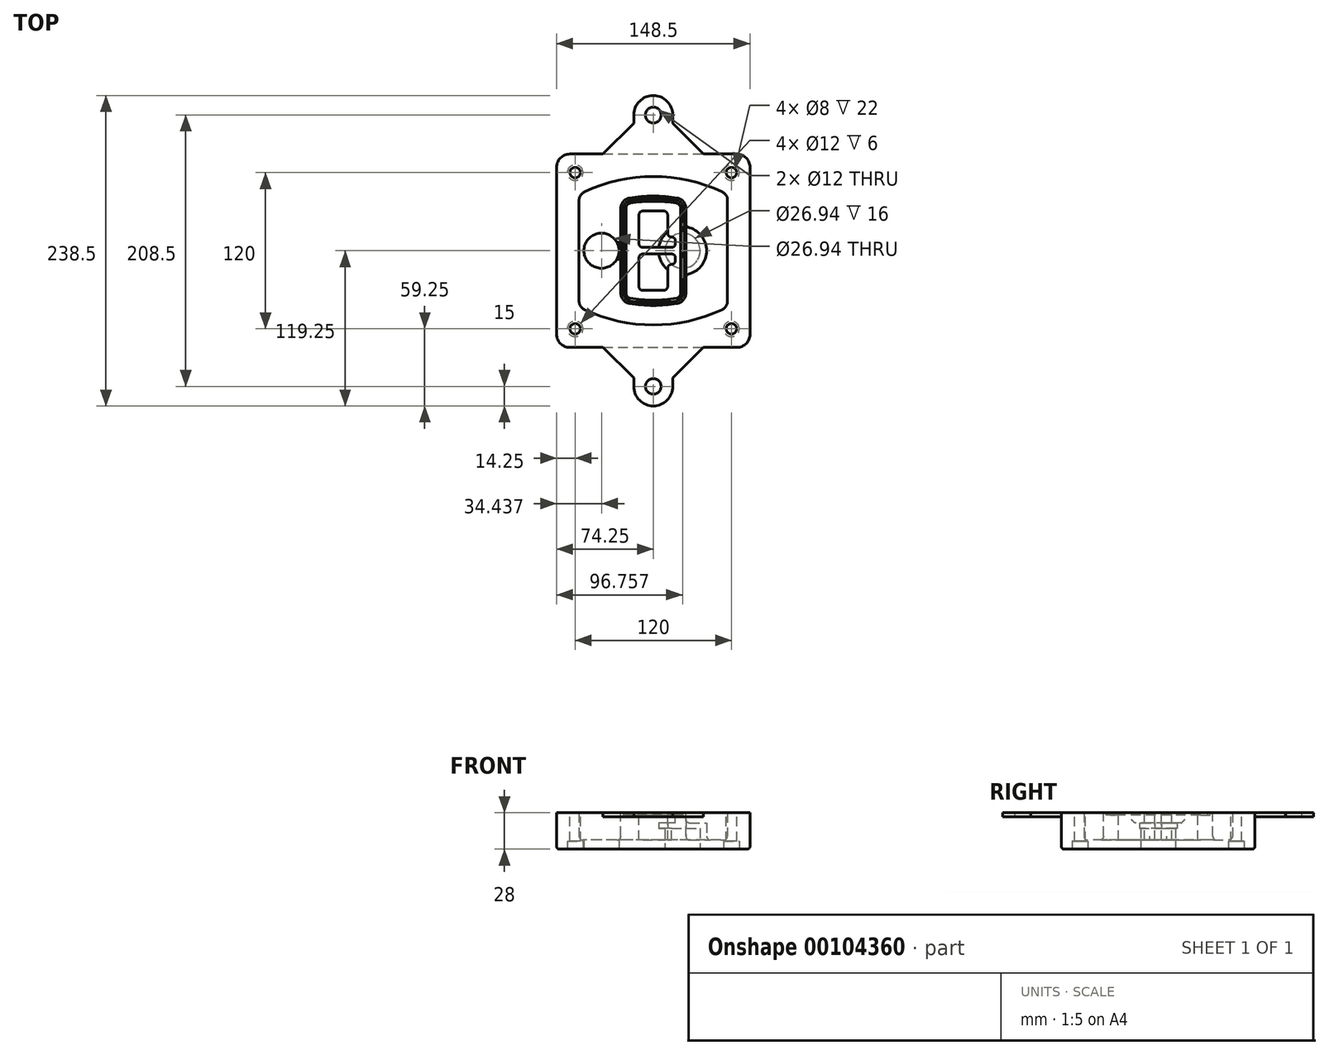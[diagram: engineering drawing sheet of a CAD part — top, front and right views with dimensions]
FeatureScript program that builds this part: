
annotation { "Feature Type Name" : "Feature", "Feature Type Description" : "" }
export const myFeature = defineFeature(function(context is Context, id is Id, definition is map)
    precondition{}
    {
        {
            var Q0;
            Q0=qCreatedBy(makeId("Top.planeOp"),FACE);
            var sketch = newSketch(context, id + "F0", { "sketchPlane" : qUnion([Q0])});
            skPoint(sketch, "E0.rect.middle", {"position": v(0, 0) * mm});
            skLineSegment(sketch, "E1.bottom", {"start": v(-64.25, -74.25) * mm, "end": v(64.25, -74.25) * mm});
            skLineSegment(sketch, "E1.top", {"start": v(-64.25, 74.25) * mm, "end": v(64.25, 74.25) * mm});
            skLineSegment(sketch, "E1.left", {"start": v(-74.25, -64.25) * mm, "end": v(-74.25, 64.25) * mm});
            skLineSegment(sketch, "E1.right", {"start": v(74.25, -64.25) * mm, "end": v(74.25, 64.25) * mm});
            skLineSegment(sketch, "E2", {"start": v(-74.25, 74.25) * mm, "end": v(74.25, -74.25) * mm, "construction": true});
            skLineSegment(sketch, "E3", {"start": v(74.25, 74.25) * mm, "end": v(-74.25, -74.25) * mm, "construction": true});
            skCircle(sketch, "E4", {"center": v(-60, 60) * mm, "radius": 4 * mm});
            skCircle(sketch, "E5", {"center": v(60, 60) * mm, "radius": 4 * mm});
            skCircle(sketch, "E6", {"center": v(60, -60) * mm, "radius": 4 * mm});
            skCircle(sketch, "E7", {"center": v(-60, -60) * mm, "radius": 4 * mm});
            skLineSegment(sketch, "E8", {"start": v(-60, 60) * mm, "end": v(60, 60) * mm, "construction": true});
            skLineSegment(sketch, "E9", {"start": v(60, 60) * mm, "end": v(60, -60) * mm, "construction": true});
            skLineSegment(sketch, "E10", {"start": v(60, -60) * mm, "end": v(-60, -60) * mm, "construction": true});
            skLineSegment(sketch, "E11", {"start": v(-60, -60) * mm, "end": v(-60, 60) * mm, "construction": true});
            skLineSegment(sketch, "E12", {"start": v(-60, 38.83) * mm, "end": v(-60, -38.83) * mm});
            skLineSegment(sketch, "E13", {"start": v(60, 38.83) * mm, "end": v(60, -38.83) * mm});
            skArc(sketch, "E14", {"start": v(54.26, 47.88) * mm, "mid": v(0, 60) * mm, "end": v(-54.26, 47.88) * mm});
            skArc(sketch, "E15", {"start": v(-54.26, -47.88) * mm, "mid": v(0, -60) * mm, "end": v(54.26, -47.88) * mm});
            skLineSegment(sketch, "E16", {"start": v(-60, 0) * mm, "end": v(60, 0) * mm, "construction": true});
            skPoint(sketch, "E17.visualSharp", {"position": v(-60, -45) * mm});
            skArc(sketch, "E17.filletArc", {"start": v(-60, -38.83) * mm, "mid": v(-58.44, -44.2) * mm, "end": v(-54.26, -47.88) * mm});
            skPoint(sketch, "E18.visualSharp", {"position": v(-60, 45) * mm});
            skArc(sketch, "E18.filletArc", {"start": v(-54.26, 47.88) * mm, "mid": v(-58.44, 44.2) * mm, "end": v(-60, 38.83) * mm});
            skPoint(sketch, "E19.visualSharp", {"position": v(60, 45) * mm});
            skArc(sketch, "E19.filletArc", {"start": v(60, 38.83) * mm, "mid": v(58.44, 44.2) * mm, "end": v(54.26, 47.88) * mm});
            skPoint(sketch, "E20.visualSharp", {"position": v(60, -45) * mm});
            skArc(sketch, "E20.filletArc", {"start": v(54.26, -47.88) * mm, "mid": v(58.44, -44.2) * mm, "end": v(60, -38.83) * mm});
            skPoint(sketch, "E21.visualSharp", {"position": v(-74.25, 74.25) * mm});
            skArc(sketch, "E21.filletArc", {"start": v(-64.25, 74.25) * mm, "mid": v(-71.32, 71.32) * mm, "end": v(-74.25, 64.25) * mm});
            skPoint(sketch, "E22.visualSharp", {"position": v(74.25, 74.25) * mm});
            skArc(sketch, "E22.filletArc", {"start": v(74.25, 64.25) * mm, "mid": v(71.32, 71.32) * mm, "end": v(64.25, 74.25) * mm});
            skPoint(sketch, "E23.visualSharp", {"position": v(74.25, -74.25) * mm});
            skArc(sketch, "E23.filletArc", {"start": v(64.25, -74.25) * mm, "mid": v(71.32, -71.32) * mm, "end": v(74.25, -64.25) * mm});
            skPoint(sketch, "E24.visualSharp", {"position": v(-74.25, -74.25) * mm});
            skArc(sketch, "E24.filletArc", {"start": v(-74.25, -64.25) * mm, "mid": v(-71.32, -71.32) * mm, "end": v(-64.25, -74.25) * mm});
            skArc(sketch, "E25.0", {"start": v(57, 38.83) * mm, "mid": v(55.9, 42.58) * mm, "end": v(52.98, 45.17) * mm});
            skLineSegment(sketch, "E25.1", {"start": v(57, 38.83) * mm, "end": v(57, -38.83) * mm});
            skArc(sketch, "E25.2", {"start": v(52.98, -45.17) * mm, "mid": v(55.9, -42.58) * mm, "end": v(57, -38.83) * mm});
            skArc(sketch, "E25.3", {"start": v(-52.98, -45.17) * mm, "mid": v(0, -57) * mm, "end": v(52.98, -45.17) * mm});
            skArc(sketch, "E25.4", {"start": v(-57, -38.83) * mm, "mid": v(-55.9, -42.58) * mm, "end": v(-52.98, -45.17) * mm});
            skArc(sketch, "E25.5", {"start": v(52.98, 45.17) * mm, "mid": v(0, 57) * mm, "end": v(-52.98, 45.17) * mm});
            skLineSegment(sketch, "E25.6", {"start": v(-57, 38.83) * mm, "end": v(-57, -38.83) * mm});
            skArc(sketch, "E25.7", {"start": v(-52.98, 45.17) * mm, "mid": v(-55.9, 42.58) * mm, "end": v(-57, 38.83) * mm});
            skArc(sketch, "E26.0", {"start": v(-55.96, 51.5) * mm, "mid": v(-61.82, 46.33) * mm, "end": v(-64, 38.83) * mm});
            skArc(sketch, "E26.1", {"start": v(55.96, 51.5) * mm, "mid": v(0, 64) * mm, "end": v(-55.96, 51.5) * mm});
            skArc(sketch, "E26.2", {"start": v(64, 38.83) * mm, "mid": v(61.82, 46.33) * mm, "end": v(55.96, 51.5) * mm});
            skLineSegment(sketch, "E26.3", {"start": v(64, 38.83) * mm, "end": v(64, -38.83) * mm});
            skArc(sketch, "E26.4", {"start": v(55.96, -51.5) * mm, "mid": v(61.82, -46.33) * mm, "end": v(64, -38.83) * mm});
            skLineSegment(sketch, "E26.5", {"start": v(-64, 38.83) * mm, "end": v(-64, -38.83) * mm});
            skArc(sketch, "E26.6", {"start": v(-55.96, -51.5) * mm, "mid": v(0, -64) * mm, "end": v(55.96, -51.5) * mm});
            skArc(sketch, "E26.7", {"start": v(-64, -38.83) * mm, "mid": v(-61.82, -46.33) * mm, "end": v(-55.96, -51.5) * mm});
            skSolve(sketch);
        }
        {
            var Q0;
            Q0=makeQuery(id+"F0.imprint","IMPRINT",FACE,{"disambiguationData":[TD([[makeQuery(id+"F0.imprint","IMPRINT",EDGE,{"derivedFrom":sQuery(id+"F0.wireOp",EDGE,"E1.bottom")}),1.0]])]});
            var Q1;
            Q1=makeQuery(id+"F0.imprint","IMPRINT",FACE,{"disambiguationData":[TD([[makeQuery(id+"F0.imprint","IMPRINT",EDGE,{"derivedFrom":sQuery(id+"F0.wireOp",EDGE,"E12")}),1.0]])]});
            var Q2;
            Q2=makeQuery(id+"F0.imprint","IMPRINT",FACE,{"disambiguationData":[TD([[makeQuery(id+"F0.imprint","IMPRINT",EDGE,{"derivedFrom":sQuery(id+"F0.wireOp",EDGE,"E25.0")}),1.0]])]});
            var Q3;
            Q3=makeQuery(id+"F0.imprint","IMPRINT",FACE,{"disambiguationData":[TD([[makeQuery(id+"F0.imprint","IMPRINT",EDGE,{"derivedFrom":sQuery(id+"F0.wireOp",EDGE,"E12")}),-1.0]])]});
            extrude(context, id + "F1", {"entities" : qUnion([Q0, Q1, Q2, Q3]), "oppositeDirection" : true, "depth" : 25 * mm});
        }
        {
            var Q0;
            Q0=makeQuery(id+"F0.imprint","IMPRINT",FACE,{"disambiguationData":[TD([[makeQuery(id+"F0.imprint","IMPRINT",EDGE,{"derivedFrom":sQuery(id+"F0.wireOp",EDGE,"E12")}),1.0]])]});
            extrude(context, id + "F2", {"entities" : qUnion([Q0]), "operationType" : NewBodyOperationType.ADD, "depth" : 3 * mm});
        }
        {
            var Q0;
            Q0=makeQuery(id+"F0.imprint","IMPRINT",FACE,{"disambiguationData":[TD([[makeQuery(id+"F0.imprint","IMPRINT",EDGE,{"derivedFrom":sQuery(id+"F0.wireOp",EDGE,"E25.0")}),1.0]])]});
            extrude(context, id + "F3", {"entities" : qUnion([Q0]), "operationType" : NewBodyOperationType.REMOVE, "oppositeDirection" : true, "depth" : 18 * mm});
        }
        {
            var Q0;
            Q0=makeQuery(id+"F2.opExtrude","CAP_FACE",FACE,{"disambiguationData":[OSD([sQuery(id+"F0.wireOp",EDGE,"E12"),sQuery(id+"F0.wireOp",EDGE,"E13"),sQuery(id+"F0.wireOp",EDGE,"E14"),sQuery(id+"F0.wireOp",EDGE,"E15"),sQuery(id+"F0.wireOp",EDGE,"E17.filletArc"),sQuery(id+"F0.wireOp",EDGE,"E18.filletArc"),sQuery(id+"F0.wireOp",EDGE,"E19.filletArc"),sQuery(id+"F0.wireOp",EDGE,"E20.filletArc"),sQuery(id+"F0.wireOp",EDGE,"E25.0"),sQuery(id+"F0.wireOp",EDGE,"E25.1"),sQuery(id+"F0.wireOp",EDGE,"E25.2"),sQuery(id+"F0.wireOp",EDGE,"E25.3"),sQuery(id+"F0.wireOp",EDGE,"E25.4"),sQuery(id+"F0.wireOp",EDGE,"E25.5"),sQuery(id+"F0.wireOp",EDGE,"E25.6"),sQuery(id+"F0.wireOp",EDGE,"E25.7")])],"isStart":false});
            var sketch = newSketch(context, id + "F4", { "sketchPlane" : qUnion([Q0])});
            skArc(sketch, "E27.0", {"start": v(-18.34, -40.45) * mm, "mid": v(0, -42) * mm, "end": v(18.34, -40.45) * mm});
            skArc(sketch, "E28.0", {"start": v(18.34, 40.45) * mm, "mid": v(0, 42) * mm, "end": v(-18.34, 40.45) * mm});
            skLineSegment(sketch, "E29", {"start": v(-25, 32.57) * mm, "end": v(-25, -32.57) * mm});
            skLineSegment(sketch, "E30", {"start": v(25, 32.57) * mm, "end": v(25, -32.57) * mm});
            skLineSegment(sketch, "E31", {"start": v(-25, 39.1) * mm, "end": v(25, 39.1) * mm, "construction": true});
            skLineSegment(sketch, "E32", {"start": v(-25, -39.1) * mm, "end": v(25, -39.1) * mm, "construction": true});
            skPoint(sketch, "E33.visualSharp", {"position": v(-25, 39.1) * mm});
            skArc(sketch, "E33.filletArc", {"start": v(-18.34, 40.45) * mm, "mid": v(-23.11, 37.73) * mm, "end": v(-25, 32.57) * mm});
            skPoint(sketch, "E34.visualSharp", {"position": v(25, 39.1) * mm});
            skArc(sketch, "E34.filletArc", {"start": v(25, 32.57) * mm, "mid": v(23.11, 37.73) * mm, "end": v(18.34, 40.45) * mm});
            skPoint(sketch, "E35.visualSharp", {"position": v(25, -39.1) * mm});
            skArc(sketch, "E35.filletArc", {"start": v(18.34, -40.45) * mm, "mid": v(23.11, -37.73) * mm, "end": v(25, -32.57) * mm});
            skPoint(sketch, "E36.visualSharp", {"position": v(-25, -39.1) * mm});
            skArc(sketch, "E36.filletArc", {"start": v(-25, -32.57) * mm, "mid": v(-23.11, -37.73) * mm, "end": v(-18.34, -40.45) * mm});
            skArc(sketch, "E37.0", {"start": v(52.98, 45.17) * mm, "mid": v(0, 57) * mm, "end": v(-52.98, 45.17) * mm});
            skArc(sketch, "E37.1", {"start": v(-52.98, 45.17) * mm, "mid": v(-55.9, 42.58) * mm, "end": v(-57, 38.83) * mm});
            skLineSegment(sketch, "E37.2", {"start": v(-57, 38.83) * mm, "end": v(-57, -38.83) * mm});
            skArc(sketch, "E37.3", {"start": v(-57, -38.83) * mm, "mid": v(-55.9, -42.58) * mm, "end": v(-52.98, -45.17) * mm});
            skArc(sketch, "E37.4", {"start": v(-52.98, -45.17) * mm, "mid": v(0, -57) * mm, "end": v(52.98, -45.17) * mm});
            skArc(sketch, "E37.5", {"start": v(52.98, -45.17) * mm, "mid": v(55.9, -42.58) * mm, "end": v(57, -38.83) * mm});
            skLineSegment(sketch, "E37.6", {"start": v(57, 38.83) * mm, "end": v(57, -38.83) * mm});
            skArc(sketch, "E37.7", {"start": v(57, 38.83) * mm, "mid": v(55.9, 42.58) * mm, "end": v(52.98, 45.17) * mm});
            skLineSegment(sketch, "E38.0", {"start": v(23, 32.57) * mm, "end": v(23, -32.57) * mm});
            skArc(sketch, "E38.1", {"start": v(18, -38.48) * mm, "mid": v(21.58, -36.44) * mm, "end": v(23, -32.57) * mm});
            skArc(sketch, "E38.2", {"start": v(-18, -38.48) * mm, "mid": v(0, -40) * mm, "end": v(18, -38.48) * mm});
            skArc(sketch, "E38.3", {"start": v(-23, -32.57) * mm, "mid": v(-21.58, -36.44) * mm, "end": v(-18, -38.48) * mm});
            skLineSegment(sketch, "E38.4", {"start": v(-23, 32.57) * mm, "end": v(-23, -32.57) * mm});
            skArc(sketch, "E38.5", {"start": v(23, 32.57) * mm, "mid": v(21.58, 36.44) * mm, "end": v(18, 38.48) * mm});
            skArc(sketch, "E38.6", {"start": v(-18, 38.48) * mm, "mid": v(-21.58, 36.44) * mm, "end": v(-23, 32.57) * mm});
            skArc(sketch, "E38.7", {"start": v(18, 38.48) * mm, "mid": v(0, 40) * mm, "end": v(-18, 38.48) * mm});
            skArc(sketch, "E39.0", {"start": v(21, 32.57) * mm, "mid": v(20.06, 35.15) * mm, "end": v(17.67, 36.5) * mm});
            skLineSegment(sketch, "E39.1", {"start": v(21, 32.57) * mm, "end": v(21, -32.57) * mm});
            skArc(sketch, "E39.2", {"start": v(17.67, -36.5) * mm, "mid": v(20.06, -35.15) * mm, "end": v(21, -32.57) * mm});
            skArc(sketch, "E39.3", {"start": v(-17.67, -36.5) * mm, "mid": v(0, -38) * mm, "end": v(17.67, -36.5) * mm});
            skArc(sketch, "E39.4", {"start": v(-21, -32.57) * mm, "mid": v(-20.06, -35.15) * mm, "end": v(-17.67, -36.5) * mm});
            skArc(sketch, "E39.5", {"start": v(17.67, 36.5) * mm, "mid": v(0, 38) * mm, "end": v(-17.67, 36.5) * mm});
            skLineSegment(sketch, "E39.6", {"start": v(-21, 32.57) * mm, "end": v(-21, -32.57) * mm});
            skArc(sketch, "E39.7", {"start": v(-17.67, 36.5) * mm, "mid": v(-20.06, 35.15) * mm, "end": v(-21, 32.57) * mm});
            skLineSegment(sketch, "E40", {"start": v(-25, 0) * mm, "end": v(25, 0) * mm, "construction": true});
            skLineSegment(sketch, "E41", {"start": v(-11, 5.5) * mm, "end": v(-11, 27.5) * mm});
            skLineSegment(sketch, "E42", {"start": v(-8, 30.5) * mm, "end": v(8, 30.5) * mm});
            skLineSegment(sketch, "E43", {"start": v(11, 27.5) * mm, "end": v(11, 13.5) * mm});
            skLineSegment(sketch, "E44", {"start": v(14, 10.5) * mm, "end": v(14, 10.5) * mm});
            skLineSegment(sketch, "E45", {"start": v(17, 7.5) * mm, "end": v(17, 5.5) * mm});
            skLineSegment(sketch, "E46", {"start": v(14, 2.5) * mm, "end": v(-8, 2.5) * mm});
            skPoint(sketch, "E47.visualSharp", {"position": v(-11, 30.5) * mm});
            skArc(sketch, "E47.filletArc", {"start": v(-8, 30.5) * mm, "mid": v(-10.12, 29.62) * mm, "end": v(-11, 27.5) * mm});
            skPoint(sketch, "E48.visualSharp", {"position": v(11, 30.5) * mm});
            skArc(sketch, "E48.filletArc", {"start": v(11, 27.5) * mm, "mid": v(10.12, 29.62) * mm, "end": v(8, 30.5) * mm});
            skPoint(sketch, "E49.visualSharp", {"position": v(11, 10.5) * mm});
            skArc(sketch, "E49.filletArc", {"start": v(11, 13.5) * mm, "mid": v(11.88, 11.38) * mm, "end": v(14, 10.5) * mm});
            skPoint(sketch, "E50.visualSharp", {"position": v(17, 10.5) * mm});
            skArc(sketch, "E50.filletArc", {"start": v(17, 7.5) * mm, "mid": v(16.12, 9.62) * mm, "end": v(14, 10.5) * mm});
            skPoint(sketch, "E51.visualSharp", {"position": v(17, 2.5) * mm});
            skArc(sketch, "E51.filletArc", {"start": v(14, 2.5) * mm, "mid": v(16.12, 3.38) * mm, "end": v(17, 5.5) * mm});
            skPoint(sketch, "E52.visualSharp", {"position": v(-11, 2.5) * mm});
            skArc(sketch, "E52.filletArc", {"start": v(-11, 5.5) * mm, "mid": v(-10.12, 3.38) * mm, "end": v(-8, 2.5) * mm});
            skLineSegment(sketch, "E53.0.MirrorCS", {"start": v(14, -2.5) * mm, "end": v(-8, -2.5) * mm});
            skArc(sketch, "E54.0.MirrorCS", {"start": v(-11, -5.5) * mm, "mid": v(-10.12, -3.38) * mm, "end": v(-8, -2.5) * mm});
            skLineSegment(sketch, "E55.0.MirrorCS", {"start": v(-11, -5.5) * mm, "end": v(-11, -27.5) * mm});
            skArc(sketch, "E56.0.MirrorCS", {"start": v(-8, -30.5) * mm, "mid": v(-10.12, -29.62) * mm, "end": v(-11, -27.5) * mm});
            skLineSegment(sketch, "E57.0.MirrorCS", {"start": v(-8, -30.5) * mm, "end": v(8, -30.5) * mm});
            skArc(sketch, "E58.0.MirrorCS", {"start": v(11, -27.5) * mm, "mid": v(10.12, -29.62) * mm, "end": v(8, -30.5) * mm});
            skLineSegment(sketch, "E59.0.MirrorCS", {"start": v(11, -27.5) * mm, "end": v(11, -13.5) * mm});
            skArc(sketch, "E60.0.MirrorCS", {"start": v(11, -13.5) * mm, "mid": v(11.88, -11.38) * mm, "end": v(14, -10.5) * mm});
            skArc(sketch, "E61.0.MirrorCS", {"start": v(17, -7.5) * mm, "mid": v(16.12, -9.62) * mm, "end": v(14, -10.5) * mm});
            skLineSegment(sketch, "E62.0.MirrorCS", {"start": v(17, -7.5) * mm, "end": v(17, -5.5) * mm});
            skArc(sketch, "E63.0.MirrorCS", {"start": v(14, -2.5) * mm, "mid": v(16.12, -3.38) * mm, "end": v(17, -5.5) * mm});
            skSolve(sketch);
        }
        {
            var Q0;
            Q0=makeQuery(id+"F4.imprint","IMPRINT",FACE,{"disambiguationData":[TD([[makeQuery(id+"F4.imprint","IMPRINT",EDGE,{"derivedFrom":sQuery(id+"F4.wireOp",EDGE,"E27.0")}),1.0]])]});
            var Q1;
            Q1=makeQuery(id+"F4.imprint","IMPRINT",FACE,{"disambiguationData":[TD([[makeQuery(id+"F4.imprint","IMPRINT",EDGE,{"derivedFrom":sQuery(id+"F4.wireOp",EDGE,"E38.0")}),-1.0]])]});
            var Q2;
            Q2=makeQuery(id+"F4.imprint","IMPRINT",FACE,{"disambiguationData":[TD([[makeQuery(id+"F4.imprint","IMPRINT",EDGE,{"derivedFrom":sQuery(id+"F4.wireOp",EDGE,"E39.0")}),1.0]])]});
            extrude(context, id + "F5", {"entities" : qUnion([Q0, Q1, Q2]), "operationType" : NewBodyOperationType.ADD, "endBound" : BoundingType.UP_TO_NEXT, "oppositeDirection" : true, "depth" : 25 * mm});
        }
        {
            var Q0;
            Q0=makeQuery(id+"F4.imprint","IMPRINT",FACE,{"disambiguationData":[TD([[makeQuery(id+"F4.imprint","IMPRINT",EDGE,{"derivedFrom":sQuery(id+"F4.wireOp",EDGE,"E38.0")}),-1.0]])]});
            extrude(context, id + "F6", {"entities" : qUnion([Q0]), "operationType" : NewBodyOperationType.REMOVE, "oppositeDirection" : true, "depth" : 2 * mm});
        }
        {
            var Q0;
            Q0=makeQuery(id+"F1.opExtrude","CAP_FACE",FACE,{"disambiguationData":[OSD([sQuery(id+"F0.wireOp",EDGE,"E1.bottom"),sQuery(id+"F0.wireOp",EDGE,"E1.top"),sQuery(id+"F0.wireOp",EDGE,"E1.left"),sQuery(id+"F0.wireOp",EDGE,"E1.right"),sQuery(id+"F0.wireOp",EDGE,"E4"),sQuery(id+"F0.wireOp",EDGE,"E5"),sQuery(id+"F0.wireOp",EDGE,"E6"),sQuery(id+"F0.wireOp",EDGE,"E7"),sQuery(id+"F0.wireOp",EDGE,"E21.filletArc"),sQuery(id+"F0.wireOp",EDGE,"E22.filletArc"),sQuery(id+"F0.wireOp",EDGE,"E23.filletArc"),sQuery(id+"F0.wireOp",EDGE,"E24.filletArc")])],"isStart":false});
            var sketch = newSketch(context, id + "F7", { "sketchPlane" : qUnion([Q0])});
            skCircle(sketch, "E64", {"center": v(22.5, 0) * mm, "radius": 13.47 * mm});
            skCircle(sketch, "E65", {"center": v(-39.81, 0) * mm, "radius": 13.47 * mm});
            skLineSegment(sketch, "E66", {"start": v(74.25, 0) * mm, "end": v(-74.25, 0) * mm});
            skCircle(sketch, "E67", {"center": v(22.5, 0) * mm, "radius": 18.47 * mm});
            skCircle(sketch, "E68", {"center": v(60, -60) * mm, "radius": 6 * mm});
            skCircle(sketch, "E69", {"center": v(-60, -60) * mm, "radius": 6 * mm});
            skCircle(sketch, "E70", {"center": v(-60, 60) * mm, "radius": 6 * mm});
            skCircle(sketch, "E71", {"center": v(60, 60) * mm, "radius": 6 * mm});
            skSolve(sketch);
        }
        {
            var Q0;
            {var subQ1=sQuery(id+"F7.wireOp",EDGE,"E66");var subQ4=sQuery(id+"F7.wireOp",EDGE,"E64");var subQ6=makeQuery(id+"F7.imprint","INTERSECT",VERTEX,{"disambiguationData":[OD(0.0)],"derivedFrom":[subQ4,subQ1]});Q0=makeQuery(id+"F7.imprint","IMPRINT",FACE,{"disambiguationData":[TD([[makeQuery(id+"F7.imprint","IMPRINT",EDGE,{"disambiguationData":[TD([[subQ6,-1.0]])],"derivedFrom":subQ4}),-1.0]])]});}
            var Q1;
            {var subQ0=sQuery(id+"F7.wireOp",EDGE,"E66");var subQ1=sQuery(id+"F7.wireOp",EDGE,"E64");var subQ3=makeQuery(id+"F7.imprint","INTERSECT",VERTEX,{"disambiguationData":[OD(0.0)],"derivedFrom":[subQ1,subQ0]});Q1=makeQuery(id+"F7.imprint","IMPRINT",FACE,{"disambiguationData":[TD([[makeQuery(id+"F7.imprint","IMPRINT",EDGE,{"disambiguationData":[TD([[subQ3,-1.0]])],"derivedFrom":subQ1}),1.0]])]});}
            var Q2;
            {var subQ0=sQuery(id+"F7.wireOp",EDGE,"E66");var subQ1=sQuery(id+"F7.wireOp",EDGE,"E64");var subQ3=makeQuery(id+"F7.imprint","INTERSECT",VERTEX,{"disambiguationData":[OD(0.0)],"derivedFrom":[subQ1,subQ0]});Q2=makeQuery(id+"F7.imprint","IMPRINT",FACE,{"disambiguationData":[TD([[makeQuery(id+"F7.imprint","IMPRINT",EDGE,{"disambiguationData":[TD([[subQ3,1.0]])],"derivedFrom":subQ1}),1.0]])]});}
            var Q3;
            {var subQ1=sQuery(id+"F7.wireOp",EDGE,"E66");var subQ4=sQuery(id+"F7.wireOp",EDGE,"E64");var subQ6=makeQuery(id+"F7.imprint","INTERSECT",VERTEX,{"disambiguationData":[OD(0.0)],"derivedFrom":[subQ4,subQ1]});Q3=makeQuery(id+"F7.imprint","IMPRINT",FACE,{"disambiguationData":[TD([[makeQuery(id+"F7.imprint","IMPRINT",EDGE,{"disambiguationData":[TD([[subQ6,1.0]])],"derivedFrom":subQ4}),-1.0]])]});}
            extrude(context, id + "F8", {"entities" : qUnion([Q0, Q1, Q2, Q3]), "operationType" : NewBodyOperationType.ADD, "oppositeDirection" : true, "depth" : 20 * mm});
        }
        {
            var Q0;
            {var subQ0=sQuery(id+"F7.wireOp",EDGE,"E66");var subQ1=sQuery(id+"F7.wireOp",EDGE,"E64");var subQ3=makeQuery(id+"F7.imprint","INTERSECT",VERTEX,{"disambiguationData":[OD(0.0)],"derivedFrom":[subQ1,subQ0]});Q0=makeQuery(id+"F7.imprint","IMPRINT",FACE,{"disambiguationData":[TD([[makeQuery(id+"F7.imprint","IMPRINT",EDGE,{"disambiguationData":[TD([[subQ3,-1.0]])],"derivedFrom":subQ1}),1.0]])]});}
            var Q1;
            {var subQ0=sQuery(id+"F7.wireOp",EDGE,"E66");var subQ1=sQuery(id+"F7.wireOp",EDGE,"E64");var subQ3=makeQuery(id+"F7.imprint","INTERSECT",VERTEX,{"disambiguationData":[OD(0.0)],"derivedFrom":[subQ1,subQ0]});Q1=makeQuery(id+"F7.imprint","IMPRINT",FACE,{"disambiguationData":[TD([[makeQuery(id+"F7.imprint","IMPRINT",EDGE,{"disambiguationData":[TD([[subQ3,1.0]])],"derivedFrom":subQ1}),1.0]])]});}
            extrude(context, id + "F9", {"entities" : qUnion([Q0, Q1]), "operationType" : NewBodyOperationType.REMOVE, "oppositeDirection" : true, "depth" : 16 * mm});
        }
        {
            var Q0;
            {var subQ0=sQuery(id+"F7.wireOp",EDGE,"E66");var subQ1=sQuery(id+"F7.wireOp",EDGE,"E65");var subQ3=makeQuery(id+"F7.imprint","INTERSECT",VERTEX,{"disambiguationData":[OD(0.0)],"derivedFrom":[subQ1,subQ0]});Q0=makeQuery(id+"F7.imprint","IMPRINT",FACE,{"disambiguationData":[TD([[makeQuery(id+"F7.imprint","IMPRINT",EDGE,{"disambiguationData":[TD([[subQ3,-1.0]])],"derivedFrom":subQ1}),1.0]])]});}
            var Q1;
            {var subQ0=sQuery(id+"F7.wireOp",EDGE,"E66");var subQ1=sQuery(id+"F7.wireOp",EDGE,"E65");var subQ3=makeQuery(id+"F7.imprint","INTERSECT",VERTEX,{"disambiguationData":[OD(0.0)],"derivedFrom":[subQ1,subQ0]});Q1=makeQuery(id+"F7.imprint","IMPRINT",FACE,{"disambiguationData":[TD([[makeQuery(id+"F7.imprint","IMPRINT",EDGE,{"disambiguationData":[TD([[subQ3,1.0]])],"derivedFrom":subQ1}),1.0]])]});}
            extrude(context, id + "F10", {"entities" : qUnion([Q0, Q1]), "operationType" : NewBodyOperationType.REMOVE, "oppositeDirection" : true, "depth" : 25 * mm});
        }
        {
            var Q0;
            Q0=makeQuery(id+"F7.imprint","IMPRINT",FACE,{"disambiguationData":[TD([[makeQuery(id+"F7.imprint","IMPRINT",EDGE,{"derivedFrom":sQuery(id+"F7.wireOp",EDGE,"E68")}),1.0]])]});
            var Q1;
            Q1=makeQuery(id+"F7.imprint","IMPRINT",FACE,{"disambiguationData":[TD([[makeQuery(id+"F7.imprint","IMPRINT",EDGE,{"derivedFrom":makeQuery(id+"F1.opExtrude","CAP_EDGE",EDGE,{"disambiguationData":[OSD([sQuery(id+"F0.wireOp",EDGE,"E5")])],"isStart":false})}),-1.0]])]});
            var Q2;
            Q2=makeQuery(id+"F7.imprint","IMPRINT",FACE,{"disambiguationData":[TD([[makeQuery(id+"F7.imprint","IMPRINT",EDGE,{"derivedFrom":sQuery(id+"F7.wireOp",EDGE,"E69")}),1.0]])]});
            var Q3;
            Q3=makeQuery(id+"F7.imprint","IMPRINT",FACE,{"disambiguationData":[TD([[makeQuery(id+"F7.imprint","IMPRINT",EDGE,{"derivedFrom":makeQuery(id+"F1.opExtrude","CAP_EDGE",EDGE,{"disambiguationData":[OSD([sQuery(id+"F0.wireOp",EDGE,"E4")])],"isStart":false})}),-1.0]])]});
            var Q4;
            Q4=makeQuery(id+"F7.imprint","IMPRINT",FACE,{"disambiguationData":[TD([[makeQuery(id+"F7.imprint","IMPRINT",EDGE,{"derivedFrom":sQuery(id+"F7.wireOp",EDGE,"E70")}),1.0]])]});
            var Q5;
            Q5=makeQuery(id+"F7.imprint","IMPRINT",FACE,{"disambiguationData":[TD([[makeQuery(id+"F7.imprint","IMPRINT",EDGE,{"derivedFrom":makeQuery(id+"F1.opExtrude","CAP_EDGE",EDGE,{"disambiguationData":[OSD([sQuery(id+"F0.wireOp",EDGE,"E7")])],"isStart":false})}),-1.0]])]});
            var Q6;
            Q6=makeQuery(id+"F7.imprint","IMPRINT",FACE,{"disambiguationData":[TD([[makeQuery(id+"F7.imprint","IMPRINT",EDGE,{"derivedFrom":sQuery(id+"F7.wireOp",EDGE,"E71")}),1.0]])]});
            var Q7;
            Q7=makeQuery(id+"F7.imprint","IMPRINT",FACE,{"disambiguationData":[TD([[makeQuery(id+"F7.imprint","IMPRINT",EDGE,{"derivedFrom":makeQuery(id+"F1.opExtrude","CAP_EDGE",EDGE,{"disambiguationData":[OSD([sQuery(id+"F0.wireOp",EDGE,"E6")])],"isStart":false})}),-1.0]])]});
            extrude(context, id + "F11", {"entities" : qUnion([Q0, Q1, Q2, Q3, Q4, Q5, Q6, Q7]), "operationType" : NewBodyOperationType.REMOVE, "oppositeDirection" : true, "depth" : 6 * mm});
        }
        {
            var Q0;
            Q0=makeQuery(id+"F9.boolean.opBoolean","COPY",FACE,{"derivedFrom":makeQuery(id+"F9.opExtrude","CAP_FACE",FACE,{"disambiguationData":[OSD([sQuery(id+"F7.wireOp",EDGE,"E64")])],"isStart":false})});
            var sketch = newSketch(context, id + "F12", { "sketchPlane" : qUnion([Q0])});
            skArc(sketch, "E72.0", {"start": v(11, 14.45) * mm, "mid": v(6.45, 9.13) * mm, "end": v(4.2, 2.5) * mm});
            skArc(sketch, "E72.1", {"start": v(4.2, -2.5) * mm, "mid": v(6.45, -9.13) * mm, "end": v(11, -14.45) * mm});
            skLineSegment(sketch, "E73", {"start": v(4.2, -2.5) * mm, "end": v(14, -2.5) * mm});
            skLineSegment(sketch, "E74.0", {"start": v(14, 2.5) * mm, "end": v(4.2, 2.5) * mm});
            skArc(sketch, "E74.1", {"start": v(14, 2.5) * mm, "mid": v(16.12, 3.38) * mm, "end": v(17, 5.5) * mm});
            skLineSegment(sketch, "E74.2", {"start": v(17, 7.5) * mm, "end": v(17, 5.5) * mm});
            skArc(sketch, "E74.3", {"start": v(17, 7.5) * mm, "mid": v(16.12, 9.62) * mm, "end": v(14, 10.5) * mm});
            skArc(sketch, "E74.4", {"start": v(11, 13.5) * mm, "mid": v(11.88, 11.38) * mm, "end": v(14, 10.5) * mm});
            skLineSegment(sketch, "E74.5", {"start": v(11, 14.45) * mm, "end": v(11, 13.5) * mm});
            skLineSegment(sketch, "E74.7", {"start": v(14, -2.5) * mm, "end": v(4.2, -2.5) * mm});
            skArc(sketch, "E74.8", {"start": v(14, -2.5) * mm, "mid": v(16.12, -3.38) * mm, "end": v(17, -5.5) * mm});
            skLineSegment(sketch, "E74.9", {"start": v(17, -7.5) * mm, "end": v(17, -5.5) * mm});
            skArc(sketch, "E74.10", {"start": v(17, -7.5) * mm, "mid": v(16.12, -9.62) * mm, "end": v(14, -10.5) * mm});
            skArc(sketch, "E74.11", {"start": v(11, -13.5) * mm, "mid": v(11.88, -11.38) * mm, "end": v(14, -10.5) * mm});
            skLineSegment(sketch, "E74.12", {"start": v(11, -14.45) * mm, "end": v(11, -13.5) * mm});
            skPoint(sketch, "E75.orphan", {"position": v(11, -27.5) * mm});
            skPoint(sketch, "E76.orphan", {"position": v(-8, -2.5) * mm});
            skPoint(sketch, "E77.orphan", {"position": v(-8, 2.5) * mm});
            skPoint(sketch, "E78.orphan", {"position": v(11, 27.5) * mm});
            skSolve(sketch);
        }
        {
            var Q0;
            {var subQ7=sQuery(id+"F12.wireOp",EDGE,"E72.0");var subQ14=sQuery(id+"F12.wireOp",EDGE,"E72.1");var subQ16=sQuery(id+"F12.wireOp",EDGE,"E74.1");var subQ18=sQuery(id+"F12.wireOp",EDGE,"E74.8");Q0=qUnion([makeQuery(id+"F12.imprint","IMPRINT",FACE,{"disambiguationData":[TD([[makeQuery(id+"F12.imprint","IMPRINT",EDGE,{"derivedFrom":subQ7}),1.0]])]}),makeQuery(id+"F12.imprint","IMPRINT",FACE,{"disambiguationData":[TD([[makeQuery(id+"F12.imprint","IMPRINT",EDGE,{"derivedFrom":subQ14}),1.0]])]}),makeQuery(id+"F12.imprint","IMPRINT",FACE,{"disambiguationData":[TD([[makeQuery(id+"F12.imprint","IMPRINT",EDGE,{"derivedFrom":subQ16}),1.0]])]}),makeQuery(id+"F12.imprint","IMPRINT",FACE,{"disambiguationData":[TD([[makeQuery(id+"F12.imprint","IMPRINT",EDGE,{"derivedFrom":subQ18}),-1.0]])]})]);}
            var Q1;
            Q1=makeQuery(id+"F5.boolean.opBoolean","SPLIT",FACE,{"disambiguationData":[TD([makeQuery(id+"F5.opExtrude","SWEPT_FACE",FACE,{"disambiguationData":[OSD([sQuery(id+"F4.wireOp",EDGE,"E41")])]})])],"derivedFrom":makeQuery(id+"F3.boolean.opBoolean","COPY",FACE,{"derivedFrom":makeQuery(id+"F3.opExtrude","CAP_FACE",FACE,{"disambiguationData":[OSD([sQuery(id+"F0.wireOp",EDGE,"E25.0"),sQuery(id+"F0.wireOp",EDGE,"E25.1"),sQuery(id+"F0.wireOp",EDGE,"E25.2"),sQuery(id+"F0.wireOp",EDGE,"E25.3"),sQuery(id+"F0.wireOp",EDGE,"E25.4"),sQuery(id+"F0.wireOp",EDGE,"E25.5"),sQuery(id+"F0.wireOp",EDGE,"E25.6"),sQuery(id+"F0.wireOp",EDGE,"E25.7")])],"isStart":false})})});
            extrude(context, id + "F13", {"entities" : qUnion([Q0]), "operationType" : NewBodyOperationType.REMOVE, "endBound" : BoundingType.UP_TO_SURFACE, "endBoundEntityFace" : qUnion([Q1]), "depth" : 25 * mm});
        }
        {
            var Q0;
            Q0=makeQuery(id+"F3.boolean.opBoolean","COPY",EDGE,{"derivedFrom":makeQuery(id+"F3.opExtrude","CAP_EDGE",EDGE,{"disambiguationData":[OSD([sQuery(id+"F0.wireOp",EDGE,"E25.6")])],"isStart":false})});
            var Q1;
            Q1=makeQuery(id+"F8.boolean.opBoolean","INTERSECT",EDGE,{"derivedFrom":[makeQuery(id+"F5.opExtrude","SWEPT_FACE",FACE,{"disambiguationData":[OSD([sQuery(id+"F4.wireOp",EDGE,"E30")])]}),makeQuery(id+"F8.opExtrude","CAP_FACE",FACE,{"disambiguationData":[OSD([sQuery(id+"F7.wireOp",EDGE,"E67")])],"isStart":false})]});
            var Q2;
            Q2=makeQuery(id+"F8.boolean.opBoolean","INTERSECT",EDGE,{"disambiguationData":[OD(1.0)],"derivedFrom":[makeQuery(id+"F5.opExtrude","SWEPT_FACE",FACE,{"disambiguationData":[OSD([sQuery(id+"F4.wireOp",EDGE,"E30")])]}),makeQuery(id+"F8.opExtrude","SWEPT_FACE",FACE,{"disambiguationData":[OSD([sQuery(id+"F7.wireOp",EDGE,"E67")])]})]});
            var Q3;
            {var subQ0=sQuery(id+"F4.wireOp",EDGE,"E30");Q3=makeQuery(id+"F8.boolean.opBoolean","SPLIT",EDGE,{"disambiguationData":[TD([makeQuery(id+"F5.opExtrude","SWEPT_FACE",FACE,{"disambiguationData":[OSD([sQuery(id+"F4.wireOp",EDGE,"E35.filletArc")])]})])],"derivedFrom":makeQuery(id+"F5.opExtrude","CAP_EDGE",EDGE,{"disambiguationData":[OSD([subQ0])],"isStart":false})});}
            var Q4;
            {var subQ0=sQuery(id+"F0.wireOp",EDGE,"E25.7");var subQ1=sQuery(id+"F0.wireOp",EDGE,"E25.1");var subQ2=sQuery(id+"F0.wireOp",EDGE,"E25.6");var subQ3=sQuery(id+"F0.wireOp",EDGE,"E25.5");var subQ4=sQuery(id+"F0.wireOp",EDGE,"E25.4");var subQ5=sQuery(id+"F0.wireOp",EDGE,"E25.0");var subQ6=sQuery(id+"F0.wireOp",EDGE,"E25.2");var subQ7=sQuery(id+"F0.wireOp",EDGE,"E25.3");Q4=makeQuery(id+"F8.boolean.opBoolean","INTERSECT",EDGE,{"derivedFrom":[makeQuery(id+"F5.boolean.opBoolean","SPLIT",FACE,{"disambiguationData":[TD([makeQuery(id+"F2.opExtrude","SWEPT_FACE",FACE,{"disambiguationData":[OSD([subQ5])]})])],"derivedFrom":makeQuery(id+"F3.boolean.opBoolean","COPY",FACE,{"derivedFrom":makeQuery(id+"F3.opExtrude","CAP_FACE",FACE,{"disambiguationData":[OSD([subQ5,subQ1,subQ6,subQ7,subQ4,subQ3,subQ2,subQ0])],"isStart":false})})}),makeQuery(id+"F8.opExtrude","SWEPT_FACE",FACE,{"disambiguationData":[OSD([sQuery(id+"F7.wireOp",EDGE,"E67")])]})]});}
            var Q5;
            Q5=makeQuery(id+"F8.boolean.opBoolean","INTERSECT",EDGE,{"disambiguationData":[OD(0.0)],"derivedFrom":[makeQuery(id+"F5.opExtrude","SWEPT_FACE",FACE,{"disambiguationData":[OSD([sQuery(id+"F4.wireOp",EDGE,"E30")])]}),makeQuery(id+"F8.opExtrude","SWEPT_FACE",FACE,{"disambiguationData":[OSD([sQuery(id+"F7.wireOp",EDGE,"E67")])]})]});
            fillet(context, id + "F14", {"entities" : qUnion([Q0, Q1, Q2, Q3, Q4, Q5]), "radius" : 3 * mm, "tangentPropagation" : true, "allowEdgeOverflow" : false});
        }
        {
            var Q0;
            Q0=makeQuery(id+"F1.opExtrude","CAP_EDGE",EDGE,{"disambiguationData":[OSD([sQuery(id+"F0.wireOp",EDGE,"E1.bottom")])],"isStart":false});
            fillet(context, id + "F15", {"entities" : qUnion([Q0]), "radius" : 2 * mm, "tangentPropagation" : true, "allowEdgeOverflow" : false});
        }
        {
            var Q0;
            {var subQ0=sQuery(id+"F0.wireOp",EDGE,"E22.filletArc");var subQ1=sQuery(id+"F0.wireOp",EDGE,"E7");var subQ2=sQuery(id+"F0.wireOp",EDGE,"E6");var subQ3=sQuery(id+"F0.wireOp",EDGE,"E5");var subQ4=sQuery(id+"F0.wireOp",EDGE,"E4");var subQ5=sQuery(id+"F0.wireOp",EDGE,"E1.bottom");var subQ6=sQuery(id+"F0.wireOp",EDGE,"E21.filletArc");var subQ7=sQuery(id+"F0.wireOp",EDGE,"E1.top");var subQ8=sQuery(id+"F0.wireOp",EDGE,"E1.left");var subQ9=sQuery(id+"F0.wireOp",EDGE,"E1.right");var subQ10=sQuery(id+"F0.wireOp",EDGE,"E23.filletArc");var subQ11=sQuery(id+"F0.wireOp",EDGE,"E24.filletArc");Q0=makeQuery(id+"F2.boolean.opBoolean","SPLIT",FACE,{"disambiguationData":[TD([makeQuery(id+"F1.opExtrude","SWEPT_FACE",FACE,{"disambiguationData":[OSD([subQ5])]})])],"derivedFrom":makeQuery(id+"F1.opExtrude","CAP_FACE",FACE,{"disambiguationData":[OSD([subQ5,subQ7,subQ8,subQ9,subQ4,subQ3,subQ2,subQ1,subQ6,subQ0,subQ10,subQ11])],"isStart":true})});}
            var sketch = newSketch(context, id + "F16", { "sketchPlane" : qUnion([Q0])});
            skLineSegment(sketch, "E79", {"start": v(0, 74.25) * mm, "end": v(0, 104.25) * mm, "construction": true});
            skCircle(sketch, "E80", {"center": v(0, 104.25) * mm, "radius": 6 * mm});
            skLineSegment(sketch, "E81", {"start": v(-38.56, 74.25) * mm, "end": v(-15, 97.81) * mm});
            skLineSegment(sketch, "E82", {"start": v(-15, 97.81) * mm, "end": v(-15, 104.25) * mm});
            skArc(sketch, "E83", {"start": v(15, 104.25) * mm, "mid": v(0, 119.25) * mm, "end": v(-15, 104.25) * mm});
            skLineSegment(sketch, "E84", {"start": v(15, 104.25) * mm, "end": v(15, 97.81) * mm});
            skLineSegment(sketch, "E85", {"start": v(15, 97.81) * mm, "end": v(38.56, 74.25) * mm});
            skLineSegment(sketch, "E86", {"start": v(-74.25, 0) * mm, "end": v(74.25, 0) * mm, "construction": true});
            skLineSegment(sketch, "E87.MirrorCS", {"start": v(-15, -97.81) * mm, "end": v(-15, -104.25) * mm});
            skLineSegment(sketch, "E88.MirrorCS", {"start": v(15, -104.25) * mm, "end": v(15, -97.81) * mm});
            skCircle(sketch, "E89.MirrorC", {"center": v(0, -104.25) * mm, "radius": 6 * mm});
            skLineSegment(sketch, "E90.MirrorCS", {"start": v(-38.56, -74.25) * mm, "end": v(-15, -97.81) * mm});
            skLineSegment(sketch, "E91.MirrorCS", {"start": v(15, -97.81) * mm, "end": v(38.56, -74.25) * mm});
            skArc(sketch, "E92.MirrorCS", {"start": v(15, -104.25) * mm, "mid": v(0, -119.25) * mm, "end": v(-15, -104.25) * mm});
            skSolve(sketch);
        }
        {
            var Q0;
            Q0=makeQuery(id+"F16.imprint","IMPRINT",FACE,{"disambiguationData":[TD([[makeQuery(id+"F16.imprint","IMPRINT",EDGE,{"derivedFrom":sQuery(id+"F16.wireOp",EDGE,"E80")}),-1.0]])]});
            var Q1;
            Q1=makeQuery(id+"F16.imprint","IMPRINT",FACE,{"disambiguationData":[TD([[makeQuery(id+"F16.imprint","IMPRINT",EDGE,{"derivedFrom":makeQuery(id+"F1.opExtrude","CAP_EDGE",EDGE,{"disambiguationData":[OSD([sQuery(id+"F0.wireOp",EDGE,"E1.left")])],"isStart":true})}),-1.0]])]});
            var Q2;
            Q2=makeQuery(id+"F16.imprint","IMPRINT",FACE,{"disambiguationData":[TD([[makeQuery(id+"F16.imprint","IMPRINT",EDGE,{"derivedFrom":sQuery(id+"F16.wireOp",EDGE,"E87.MirrorCS")}),1.0]])]});
            var Q3;
            Q3=makeQuery(id+"F2.opExtrude","CAP_FACE",FACE,{"disambiguationData":[OSD([sQuery(id+"F0.wireOp",EDGE,"E12"),sQuery(id+"F0.wireOp",EDGE,"E13"),sQuery(id+"F0.wireOp",EDGE,"E14"),sQuery(id+"F0.wireOp",EDGE,"E15"),sQuery(id+"F0.wireOp",EDGE,"E17.filletArc"),sQuery(id+"F0.wireOp",EDGE,"E18.filletArc"),sQuery(id+"F0.wireOp",EDGE,"E19.filletArc"),sQuery(id+"F0.wireOp",EDGE,"E20.filletArc"),sQuery(id+"F0.wireOp",EDGE,"E25.0"),sQuery(id+"F0.wireOp",EDGE,"E25.1"),sQuery(id+"F0.wireOp",EDGE,"E25.2"),sQuery(id+"F0.wireOp",EDGE,"E25.3"),sQuery(id+"F0.wireOp",EDGE,"E25.4"),sQuery(id+"F0.wireOp",EDGE,"E25.5"),sQuery(id+"F0.wireOp",EDGE,"E25.6"),sQuery(id+"F0.wireOp",EDGE,"E25.7")])],"isStart":false});
            extrude(context, id + "F17", {"entities" : qUnion([Q0, Q1, Q2]), "operationType" : NewBodyOperationType.ADD, "endBound" : BoundingType.UP_TO_SURFACE, "endBoundEntityFace" : qUnion([Q3]), "depth" : 25 * mm});
        }
    });
